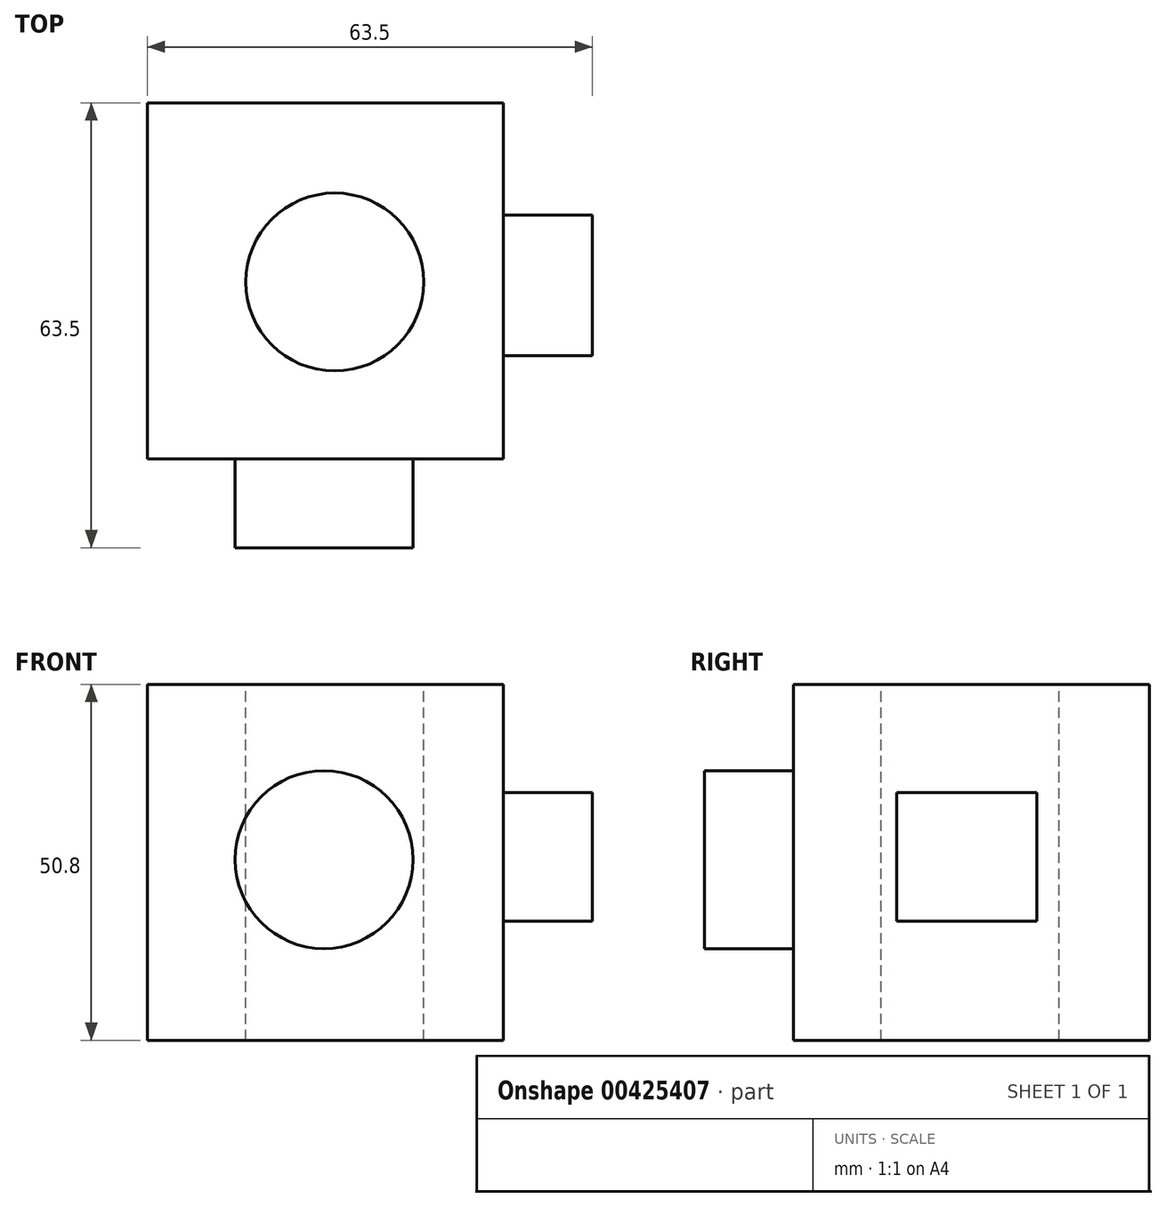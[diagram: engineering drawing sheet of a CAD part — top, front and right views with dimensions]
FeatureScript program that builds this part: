
annotation { "Feature Type Name" : "Feature", "Feature Type Description" : "" }
export const myFeature = defineFeature(function(context is Context, id is Id, definition is map)
    precondition{}
    {
        {
            var Q0;
            Q0=qCreatedBy(makeId("Front.planeOp"),FACE);
            var sketch = newSketch(context, id + "F0", { "sketchPlane" : qUnion([Q0])});
            skLineSegment(sketch, "E0.bottom", {"start": v(0, 0) * mm, "end": v(50.8, 0) * mm});
            skLineSegment(sketch, "E0.top", {"start": v(0, 50.8) * mm, "end": v(50.8, 50.8) * mm});
            skLineSegment(sketch, "E0.left", {"start": v(0, 0) * mm, "end": v(0, 50.8) * mm});
            skLineSegment(sketch, "E0.right", {"start": v(50.8, 0) * mm, "end": v(50.8, 50.8) * mm});
            skSolve(sketch);
        }
        {
            var Q0;
            Q0=makeQuery(id+"F0.imprint","IMPRINT",FACE,{"disambiguationData":[TD([[makeQuery(id+"F0.imprint","IMPRINT",EDGE,{"derivedFrom":sQuery(id+"F0.wireOp",EDGE,"E0.bottom")}),1.0]])]});
            extrude(context, id + "F1", {"entities" : qUnion([Q0]), "depth" : 50.8 * mm});
        }
        {
            var Q0;
            Q0=makeQuery(id+"F1.opExtrude","CAP_FACE",FACE,{"disambiguationData":[OSD([sQuery(id+"F0.wireOp",EDGE,"E0.bottom"),sQuery(id+"F0.wireOp",EDGE,"E0.top"),sQuery(id+"F0.wireOp",EDGE,"E0.left"),sQuery(id+"F0.wireOp",EDGE,"E0.right")])],"isStart":false});
            var sketch = newSketch(context, id + "F2", { "sketchPlane" : qUnion([Q0])});
            skCircle(sketch, "E1", {"center": v(25.2, 25.78) * mm, "radius": 12.7 * mm});
            skSolve(sketch);
        }
        {
            var Q0;
            Q0=makeQuery(id+"F2.imprint","IMPRINT",FACE,{"disambiguationData":[TD([[makeQuery(id+"F2.imprint","IMPRINT",EDGE,{"derivedFrom":sQuery(id+"F2.wireOp",EDGE,"E1")}),1.0]])]});
            extrude(context, id + "F3", {"entities" : qUnion([Q0]), "operationType" : NewBodyOperationType.ADD, "depth" : 12.7 * mm});
        }
        {
            var Q0;
            Q0=makeQuery(id+"F1.opExtrude","SWEPT_FACE",FACE,{"disambiguationData":[OSD([sQuery(id+"F0.wireOp",EDGE,"E0.right")])]});
            var sketch = newSketch(context, id + "F4", { "sketchPlane" : qUnion([Q0])});
            skLineSegment(sketch, "E2.bottom", {"start": v(-16.04, 17) * mm, "end": v(-36.1, 17) * mm});
            skLineSegment(sketch, "E2.top", {"start": v(-16.04, 35.33) * mm, "end": v(-36.1, 35.33) * mm});
            skLineSegment(sketch, "E2.left", {"start": v(-16.04, 17) * mm, "end": v(-16.04, 35.33) * mm});
            skLineSegment(sketch, "E2.right", {"start": v(-36.1, 17) * mm, "end": v(-36.1, 35.33) * mm});
            skSolve(sketch);
        }
        {
            var Q0;
            Q0=makeQuery(id+"F4.imprint","IMPRINT",FACE,{"disambiguationData":[TD([[makeQuery(id+"F4.imprint","IMPRINT",EDGE,{"derivedFrom":sQuery(id+"F4.wireOp",EDGE,"E2.bottom")}),-1.0]])]});
            extrude(context, id + "F5", {"entities" : qUnion([Q0]), "operationType" : NewBodyOperationType.ADD, "depth" : 12.7 * mm});
        }
        {
            var Q0;
            Q0=makeQuery(id+"F1.opExtrude","SWEPT_FACE",FACE,{"disambiguationData":[OSD([sQuery(id+"F0.wireOp",EDGE,"E0.top")])]});
            var sketch = newSketch(context, id + "F6", { "sketchPlane" : qUnion([Q0])});
            skCircle(sketch, "E3", {"center": v(26.73, -25.59) * mm, "radius": 12.7 * mm});
            skSolve(sketch);
        }
        {
            var Q0;
            Q0=makeQuery(id+"F6.imprint","IMPRINT",FACE,{"disambiguationData":[TD([[makeQuery(id+"F6.imprint","IMPRINT",EDGE,{"derivedFrom":sQuery(id+"F6.wireOp",EDGE,"E3")}),1.0]])]});
            extrude(context, id + "F7", {"entities" : qUnion([Q0]), "operationType" : NewBodyOperationType.REMOVE, "oppositeDirection" : true, "depth" : 50.8 * mm});
        }
    });
